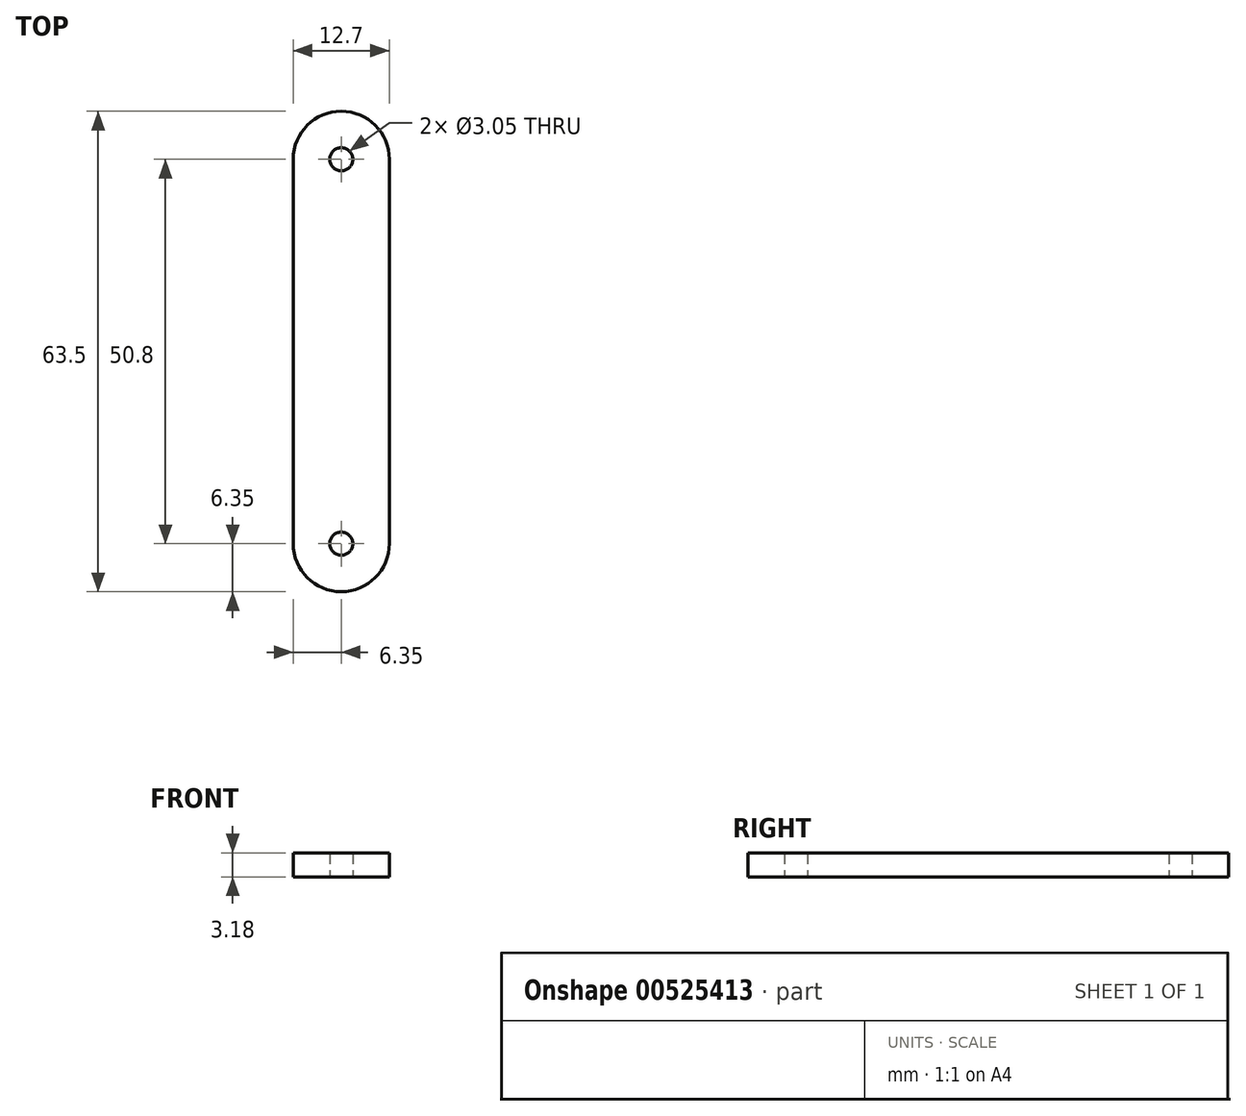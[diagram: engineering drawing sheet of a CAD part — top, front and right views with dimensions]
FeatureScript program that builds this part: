
annotation { "Feature Type Name" : "Feature", "Feature Type Description" : "" }
export const myFeature = defineFeature(function(context is Context, id is Id, definition is map)
    precondition{}
    {
        {
            var Q0;
            Q0=qCreatedBy(makeId("Top.planeOp"),FACE);
            var sketch = newSketch(context, id + "F0", { "sketchPlane" : qUnion([Q0])});
            skLineSegment(sketch, "E0.bottom", {"start": v(0, 31.75) * mm, "end": v(0, 31.75) * mm});
            skLineSegment(sketch, "E0.top", {"start": v(0, -31.75) * mm, "end": v(0, -31.75) * mm});
            skLineSegment(sketch, "E0.left", {"start": v(6.35, 25.4) * mm, "end": v(6.35, -25.4) * mm});
            skLineSegment(sketch, "E0.right", {"start": v(-6.35, 25.4) * mm, "end": v(-6.35, -25.4) * mm});
            skPoint(sketch, "E0.middle", {"position": v(0, 0) * mm});
            skCircle(sketch, "E1", {"center": v(0, -25.4) * mm, "radius": 1.52 * mm});
            skPoint(sketch, "E1.centerSnap0", {"position": v(0, -31.75) * mm});
            skCircle(sketch, "E2.MirrorC", {"center": v(0, 25.4) * mm, "radius": 1.52 * mm});
            skPoint(sketch, "E3.visualSharp", {"position": v(6.35, 31.75) * mm});
            skArc(sketch, "E3.filletArc", {"start": v(6.35, 25.4) * mm, "mid": v(4.5, 29.9) * mm, "end": v(0, 31.75) * mm});
            skPoint(sketch, "E4.visualSharp", {"position": v(-6.35, 31.75) * mm});
            skArc(sketch, "E4.filletArc", {"start": v(0, 31.75) * mm, "mid": v(-4.5, 29.9) * mm, "end": v(-6.35, 25.4) * mm});
            skPoint(sketch, "E5.visualSharp", {"position": v(-6.35, -31.75) * mm});
            skArc(sketch, "E5.filletArc", {"start": v(-6.35, -25.4) * mm, "mid": v(-4.5, -29.9) * mm, "end": v(0, -31.75) * mm});
            skPoint(sketch, "E6.visualSharp", {"position": v(6.35, -31.75) * mm});
            skArc(sketch, "E6.filletArc", {"start": v(0, -31.75) * mm, "mid": v(4.5, -29.9) * mm, "end": v(6.35, -25.4) * mm});
            skSolve(sketch);
        }
        {
            var Q0;
            Q0=makeQuery(id+"F0.imprint","IMPRINT",FACE,{"disambiguationData":[TD([[makeQuery(id+"F0.imprint","IMPRINT",EDGE,{"derivedFrom":sQuery(id+"F0.wireOp",EDGE,"E0.left")}),-1.0]])]});
            extrude(context, id + "F1", {"entities" : qUnion([Q0]), "depth" : 3.17 * mm, "offsetDistance" : 25.4 * mm});
        }
    });
